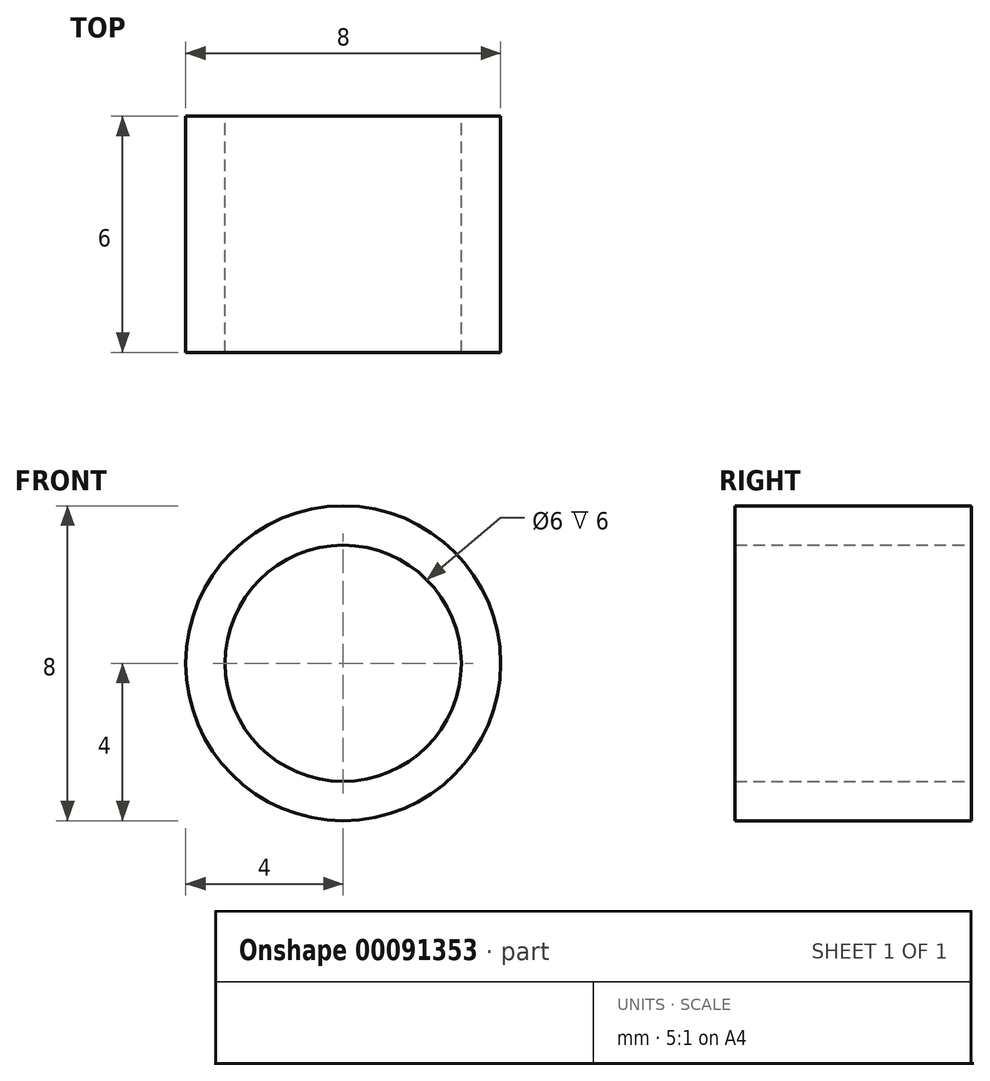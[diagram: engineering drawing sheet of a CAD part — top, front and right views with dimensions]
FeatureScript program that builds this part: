
annotation { "Feature Type Name" : "Feature", "Feature Type Description" : "" }
export const myFeature = defineFeature(function(context is Context, id is Id, definition is map)
    precondition{}
    {
        {
            var Q0;
            Q0=qCreatedBy(makeId("Front.planeOp"),FACE);
            var sketch = newSketch(context, id + "F0", { "sketchPlane" : qUnion([Q0])});
            skCircle(sketch, "E0", {"center": v(0, 0) * mm, "radius": 4 * mm});
            skSolve(sketch);
        }
        {
            var Q0;
            Q0=makeQuery(id+"F0.imprint","IMPRINT",FACE,{"disambiguationData":[TD([[makeQuery(id+"F0.imprint","IMPRINT",EDGE,{"derivedFrom":sQuery(id+"F0.wireOp",EDGE,"E0")}),1.0]])]});
            extrude(context, id + "F1", {"entities" : qUnion([Q0]), "oppositeDirection" : true, "depth" : 6 * mm});
        }
        {
            var Q0;
            Q0=sQuery(id+"F0.wireOp",VERTEX,"E0.center");
            var Q1;
            Q1=makeQuery(id+"F1.opExtrude","SWEPT_BODY",BODY,{"disambiguationData":[OSD([sQuery(id+"F0.wireOp",EDGE,"E0")])]});
            hole(context, id + "F2", {"style" : HoleStyle.SIMPLE, "endStyle" : HoleEndStyle.THROUGH, "standardTappedOrClearance" : lookupTablePath({ "standard" : "ISO", "size" : "6", "type" : "Drilled" }), "standardBlindInLast" : lookupTablePath({ "standard" : "ISO", "size" : "6", "type" : "Drilled" }), "holeDiameter" : 6 * mm, "locations" : qUnion([Q0]), "scope" : qUnion([Q1]), "isTappedThrough" : true, "startStyle" : HoleStartStyle.SKETCH});
        }
    });
